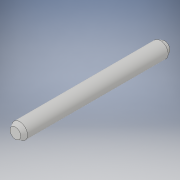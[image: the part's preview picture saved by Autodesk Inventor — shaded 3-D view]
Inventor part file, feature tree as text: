
AUTODESK INVENTOR PART (.ipt)
format: ipt  version: 2018.3 (Build 223284000, 284)  size: 103,936 bytes
history: native  units: in
note: dims shown in document units (in); Inventor stores cm internally (conversion verified against a paired STEP export)
features: revolve x1, sketch x1
ambient origin geometry x8: Origin, YZ Plane, XZ Plane, XY Plane, X Axis, Y Axis, Z Axis, Center Point
bodies: Solid1 (feature_tree)
feature tree (2):
  revolve  "Revolution1"  [1 undecoded]
  sketch  "Sketch1"  dims[d0=0.063in d1=0.6in d2=0.01in d3=60.0deg d4=0.01in d5=60.0deg d6=0.01in d7=60.0deg d8=0.01in d10=90.0deg]
note: 1 required parameter value undecoded (feature->parameter linkage not recoverable at this tier; creation-order binding heuristic only, values carry confidence <= 0.55)
